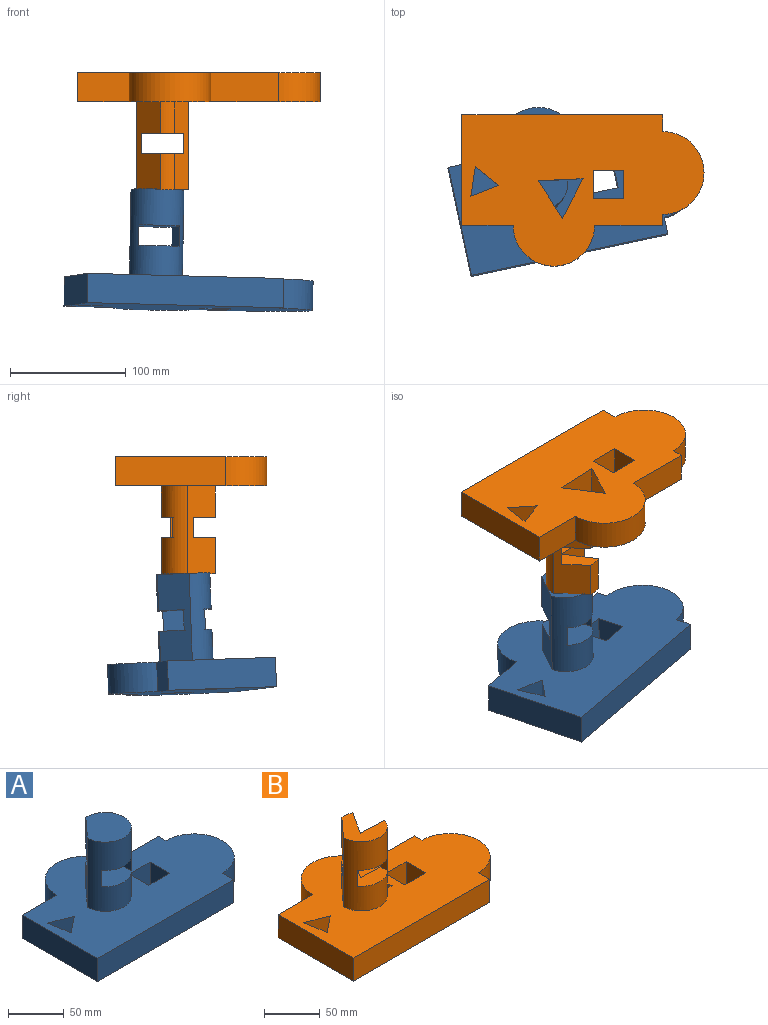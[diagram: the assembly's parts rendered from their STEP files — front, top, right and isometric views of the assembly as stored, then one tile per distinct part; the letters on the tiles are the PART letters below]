
ASSEMBLY  parts=2 mates=1
PART A: 24 faces, bbox 209.6x131x101.6 mm
  f0: cylinder r=23.22mm len=76.2mm, axis (0,0,-1), area 7338.7mm2, adj f1,f18,f19,f20,f21,f22,f23
  f1: plane 209.59x131.02mm, normal (0,0,1), area 18098.5mm2, adj f0,f3,f4,f5,f6,f7,f8,f9
  f2: plane 209.59x131.02mm, normal (0,0,-1), area 19654.5mm2, adj f3,f4,f5,f6,f7,f8,f9,f10
  f3: plane 25.4x24.28mm, normal (-0.36,-0.93,0), area 662.4mm2, adj f1,f2,f4,f13
  f4: plane 25.4x20.37mm, normal (-0.62,0.78,0), area 662.4mm2, adj f1,f2,f3,f13
  f5: cylinder r=35.86mm len=71.72mm, axis (0,0,-1), area 2861.3mm2, adj f1,f2,f6,f12
  f6: plane 25.4x9.56mm, normal (1,0,0), area 242.8mm2, adj f1,f2,f5,f7
  f7: plane 58.87x25.4mm, normal (0,1,0), area 1495.4mm2, adj f1,f2,f6,f8
  f8: cylinder r=35.31mm len=70.62mm, axis (0,0,-1), area 2817.7mm2, adj f1,f2,f7,f9
  f9: plane 44.24x25.4mm, normal (0,1,0), area 1123.7mm2, adj f1,f2,f8,f10
  f10: plane 95.71x25.4mm, normal (-1,0,0), area 2431mm2, adj f1,f2,f9,f11
  f11: plane 173.74x25.4mm, normal (0,-1,0), area 4412.9mm2, adj f1,f2,f10,f12
  f12: plane 25.4x14.43mm, normal (1,0,0), area 366.6mm2, adj f1,f2,f5,f11
  f13: plane 25.78x25.4mm, normal (0.99,0.15,0), area 662.4mm2, adj f1,f2,f3,f4
  f14: plane 26.45x25.4mm, normal (0,-1,0), area 671.9mm2, adj f1,f2,f15,f17
  f15: plane 25.4x24.84mm, normal (1,0,0), area 630.9mm2, adj f1,f2,f14,f16
  f16: plane 26.45x25.4mm, normal (0,1,0), area 671.9mm2, adj f1,f2,f15,f17
  f17: plane 25.4x24.84mm, normal (-1,0,0), area 630.9mm2, adj f1,f2,f14,f16
  f18: plane 76.2x23.59mm, normal (-0.74,0.67,0), area 1984.2mm2, adj f0,f1,f19,f21,f22,f23
  f19: plane 46.44x46.44mm, normal (0,0,1), area 1556.1mm2, adj f0,f18
  f20: plane 30.95x17.78mm, normal (-1,0,0), area 550.3mm2, adj f0,f21,f23
  f21: plane 46.44x35.79mm, normal (0,0,-1), area 1374.9mm2, adj f0,f18,f20,f22
  f22: plane 18.85x17.78mm, normal (1,0,0), area 335.2mm2, adj f0,f18,f21,f23
  f23: plane 46.44x35.79mm, normal (0,0,1), area 1374.9mm2, adj f0,f18,f20,f22
PART B: 30 faces, bbox 209.6x131x101.6 mm
  f0: cylinder r=23.22mm len=76.2mm, axis (0,0,-1), area 4211.3mm2, adj f3,f5,f6,f7,f8,f24,f25,f26
  f1: cylinder r=23.22mm len=27.13mm, axis (0,0,-1), area 327mm2, adj f3,f8,f24,f29
  f2: cylinder r=23.22mm len=31.29mm, axis (0,0,-1), area 377.2mm2, adj f5,f7,f24,f27
  f3: plane 209.59x131.02mm, normal (0,0,1), area 17988.4mm2, adj f0,f1,f9,f10,f11,f12,f13,f14
  f4: plane 209.59x131.02mm, normal (0,0,-1), area 19004.5mm2, adj f9,f10,f11,f12,f13,f14,f15,f16
  f5: plane 46.44x45.17mm, normal (0,0,1), area 1016.1mm2, adj f0,f2,f24,f26,f27
  f6: plane 17.78x8.12mm, normal (-1,0,0), area 144.4mm2, adj f0,f7,f8,f26
  f7: plane 46.44x35.79mm, normal (0,0,-1), area 938.7mm2, adj f0,f2,f6,f24,f25,f26,f27
  f8: plane 46.44x35.79mm, normal (0,0,1), area 938.7mm2, adj f0,f1,f6,f24,f25,f26,f29
  f9: plane 25.4x24.28mm, normal (-0.36,-0.93,0), area 662.4mm2, adj f3,f4,f10,f19
  f10: plane 25.4x20.37mm, normal (-0.62,0.78,0), area 662.4mm2, adj f3,f4,f9,f19
  f11: cylinder r=35.86mm len=71.72mm, axis (0,0,-1), area 2861.3mm2, adj f3,f4,f12,f18
  f12: plane 25.4x9.56mm, normal (1,0,0), area 242.8mm2, adj f3,f4,f11,f13
  f13: plane 58.87x25.4mm, normal (0,1,0), area 1495.4mm2, adj f3,f4,f12,f14
  f14: cylinder r=35.31mm len=70.62mm, axis (0,0,-1), area 2817.7mm2, adj f3,f4,f13,f15
  f15: plane 44.24x25.4mm, normal (0,1,0), area 1123.7mm2, adj f3,f4,f14,f16
  f16: plane 95.71x25.4mm, normal (-1,0,0), area 2431mm2, adj f3,f4,f15,f17
  f17: plane 173.74x25.4mm, normal (0,-1,0), area 4412.9mm2, adj f3,f4,f16,f18
  f18: plane 25.4x14.43mm, normal (1,0,0), area 366.6mm2, adj f3,f4,f11,f17
  f19: plane 25.78x25.4mm, normal (0.99,0.15,0), area 662.4mm2, adj f3,f4,f9,f10
  f20: plane 26.45x25.4mm, normal (0,-1,0), area 671.9mm2, adj f3,f4,f21,f23
  f21: plane 25.4x24.84mm, normal (1,0,0), area 630.9mm2, adj f3,f4,f20,f22
  f22: plane 26.45x25.4mm, normal (0,1,0), area 671.9mm2, adj f3,f4,f21,f23
  f23: plane 25.4x24.84mm, normal (-1,0,0), area 630.9mm2, adj f3,f4,f20,f22
  f24: plane 76.2x23.59mm, normal (-0.74,0.67,0), area 1984.2mm2, adj f0,f1,f2,f3,f5,f7,f8,f25
  f25: plane 18.85x17.78mm, normal (1,0,0), area 335.2mm2, adj f0,f7,f8,f24
  f26: plane 101.6x38.71mm, normal (0.04,1,0), area 2791.2mm2, adj f0,f3,f4,f5,f6,f7,f8,f27
  f27: plane 31.29x27.27mm, normal (0.84,-0.54,0), area 1012.2mm2, adj f2,f5,f7,f26
  f28: plane 34.38x25.4mm, normal (-0.89,-0.46,0), area 984.1mm2, adj f3,f4,f26,f29
  f29: plane 52.53x32.66mm, normal (0.84,-0.54,0), area 1861.6mm2, adj f1,f3,f4,f8,f26,f28
PLACE A rot(axis=(-0.16,0.1,0.98),12.3deg) t=(8.65,54.76,140.34)mm
PLACE B rot(axis=(1,0,0),180deg) t=(12.77,80.8,343.41)mm fixed
MATE ball B.f5 <-> A.f19  axis (0,0,-1) through (-8.13,69.11,241.81)mm
